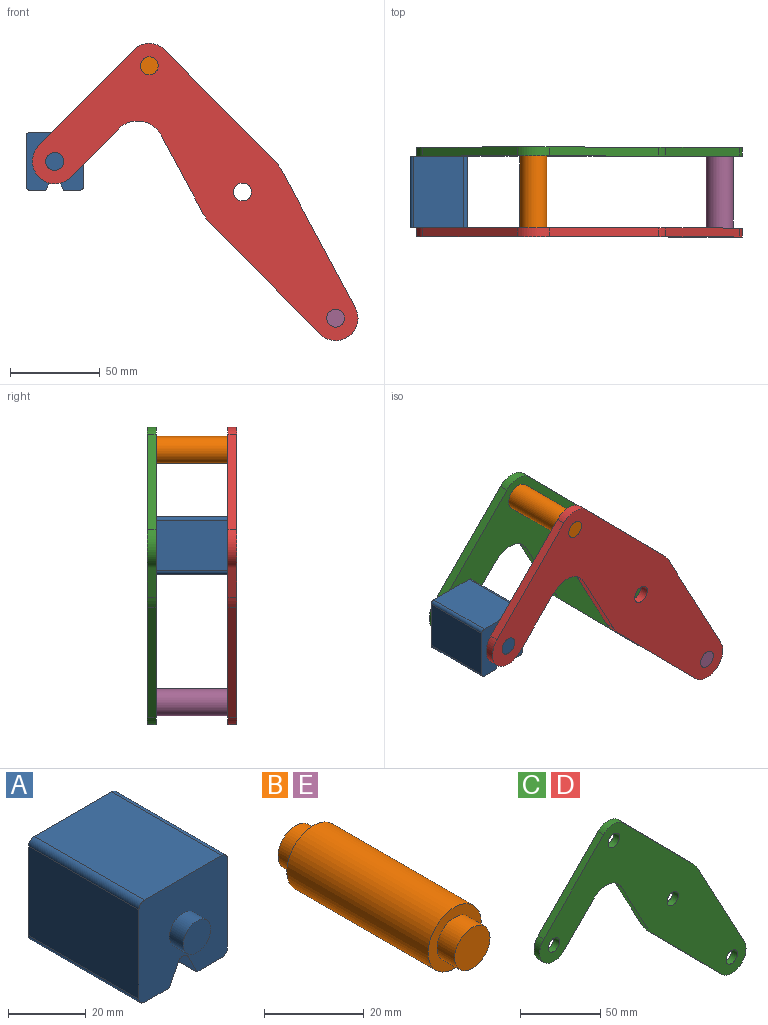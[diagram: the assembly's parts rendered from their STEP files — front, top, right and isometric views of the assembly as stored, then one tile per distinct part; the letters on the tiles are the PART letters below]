
ASSEMBLY  parts=5 mates=3
PART A: 18 faces, bbox 32.1x50x32.1 mm
  f0: plane 40x28.08mm, normal (1,0,0), area 1123.1mm2, adj f4,f10,f13,f14
  f1: plane 40x9.04mm, normal (0,0,-1), area 361.6mm2, adj f2,f4,f10,f14
  f2: plane 40x6.42mm, normal (-0.89,0,-0.45), area 287.2mm2, adj f1,f4,f10,f15
  f3: plane 40x6.42mm, normal (0.89,0,-0.45), area 287.2mm2, adj f4,f5,f10,f15
  f4: plane 32.08x32.08mm, normal (0,-1,0), area 900.6mm2, adj f0,f1,f2,f3,f5,f6,f7,f9
  f5: plane 40x9.04mm, normal (0,0,-1), area 361.6mm2, adj f3,f4,f10,f16
  f6: plane 40x28.08mm, normal (0,0,1), area 1123.1mm2, adj f4,f10,f13,f17
  f7: plane 40x28.08mm, normal (-1,0,0), area 1123.1mm2, adj f4,f10,f16,f17
  f8: plane 10x10mm, normal (0,-1,0), area 78.5mm2, adj f9
  f9: cylinder r=5mm len=10mm, axis (0,1,0), area 157.1mm2, adj f4,f8
  f10: plane 32.08x32.08mm, normal (0,1,0), area 900.6mm2, adj f0,f1,f2,f3,f5,f6,f7,f12
  f11: plane 10x10mm, normal (0,1,0), area 78.5mm2, adj f12
  f12: cylinder r=5mm len=10mm, axis (0,-1,0), area 157.1mm2, adj f10,f11
  f13: cylinder r=2mm len=40mm, axis (0,1,0), area 125.7mm2, adj f0,f4,f6,f10
  f14: cylinder r=2mm len=40mm, axis (0,-1,0), area 125.7mm2, adj f0,f1,f4,f10
  f15: cylinder r=2mm len=40mm, axis (0,1,0), area 177.1mm2, adj f2,f3,f4,f10
  f16: cylinder r=2mm len=40mm, axis (0,1,0), area 125.7mm2, adj f4,f5,f7,f10
  f17: cylinder r=2mm len=40mm, axis (0,-1,0), area 125.7mm2, adj f4,f6,f7,f10
PART B: 7 faces, bbox 15x50x15 mm
  f0: cylinder r=7.5mm len=40mm, axis (0,-1,0), area 1885mm2, adj f2,f5
  f1: cylinder r=5mm len=10mm, axis (0,1,0), area 157.1mm2, adj f2,f3
  f2: plane 15x15mm, normal (0,-1,0), area 98.2mm2, adj f0,f1
  f3: plane 10x10mm, normal (0,-1,0), area 78.5mm2, adj f1
  f4: cylinder r=5mm len=10mm, axis (0,-1,0), area 157.1mm2, adj f5,f6
  f5: plane 15x15mm, normal (0,1,0), area 98.2mm2, adj f0,f4
  f6: plane 10x10mm, normal (0,1,0), area 78.5mm2, adj f4
PART C: 18 faces, bbox 181.7x5x165.8 mm
  f0: plane 43.49x23.35mm, normal (-0.88,0,-0.47), area 246.8mm2, adj f1,f14,f16,f17
  f1: cylinder r=25mm len=5.75mm, axis (0,1,0), area 35.8mm2, adj f0,f2,f16,f17
  f2: plane 61.6x60.87mm, normal (-0.71,0,-0.7), area 433mm2, adj f1,f3,f16,f17
  f3: cylinder r=12.5mm len=21.39mm, axis (0,1,0), area 178.4mm2, adj f2,f4,f16,f17
  f4: plane 76.3x40.96mm, normal (0.88,0,0.47), area 433mm2, adj f3,f5,f16,f17
  f5: cylinder r=25mm len=5.75mm, axis (0,1,0), area 35.8mm2, adj f4,f6,f16,f17
  f6: plane 61.6x60.87mm, normal (0.71,0,0.7), area 433mm2, adj f5,f7,f16,f17
  f7: cylinder r=12.5mm len=17.78mm, axis (0,1,0), area 98.9mm2, adj f6,f8,f16,f17
  f8: plane 53.35x52.71mm, normal (-0.71,0,0.7), area 375mm2, adj f7,f9,f16,f17
  f9: cylinder r=12.5mm len=21.39mm, axis (0,1,0), area 196.3mm2, adj f8,f10,f16,f17
  f10: plane 26.86x26.54mm, normal (0.71,0,-0.7), area 188.8mm2, adj f9,f14,f16,f17
  f11: cylinder r=5mm len=10mm, axis (0,1,0), area 157.1mm2, adj f16,f17
  f12: cylinder r=5mm len=10mm, axis (0,1,0), area 157.1mm2, adj f16,f17
  f13: cylinder r=5mm len=10mm, axis (0,1,0), area 157.1mm2, adj f16,f17
  f14: cylinder r=15mm len=23.89mm, axis (0,1,0), area 140.2mm2, adj f0,f10,f16,f17
  f15: cylinder r=5mm len=10mm, axis (0,1,0), area 157.1mm2, adj f16,f17
  f16: plane 181.66x165.78mm, normal (0,-1,0), area 8710.1mm2, adj f0,f1,f2,f3,f4,f5,f6,f7
  f17: plane 181.66x165.78mm, normal (0,1,0), area 8710.1mm2, adj f0,f1,f2,f3,f4,f5,f6,f7
PART D: same geometry as C
PART E: same geometry as B
PLACE A t=(8.61,-23.1,-12.11)mm
PLACE B t=(8.61,-23.1,-12.11)mm
PLACE C t=(8.61,21.9,-12.11)mm
PLACE D t=(8.61,-23.1,-12.11)mm fixed
PLACE E t=(112.56,-23.1,-152.89)mm
MATE fastened E.f0 <-> D.f3  axis (0,-1,0) through (60.58,-28.1,-82.5)mm
MATE revolute A.f9 <-> D.f9  axis (0,-1,0) through (-96.08,-28.1,4.93)mm
MATE fastened B.f0 <-> C.f7  axis (0,1,0) through (-43.37,21.9,58.28)mm
